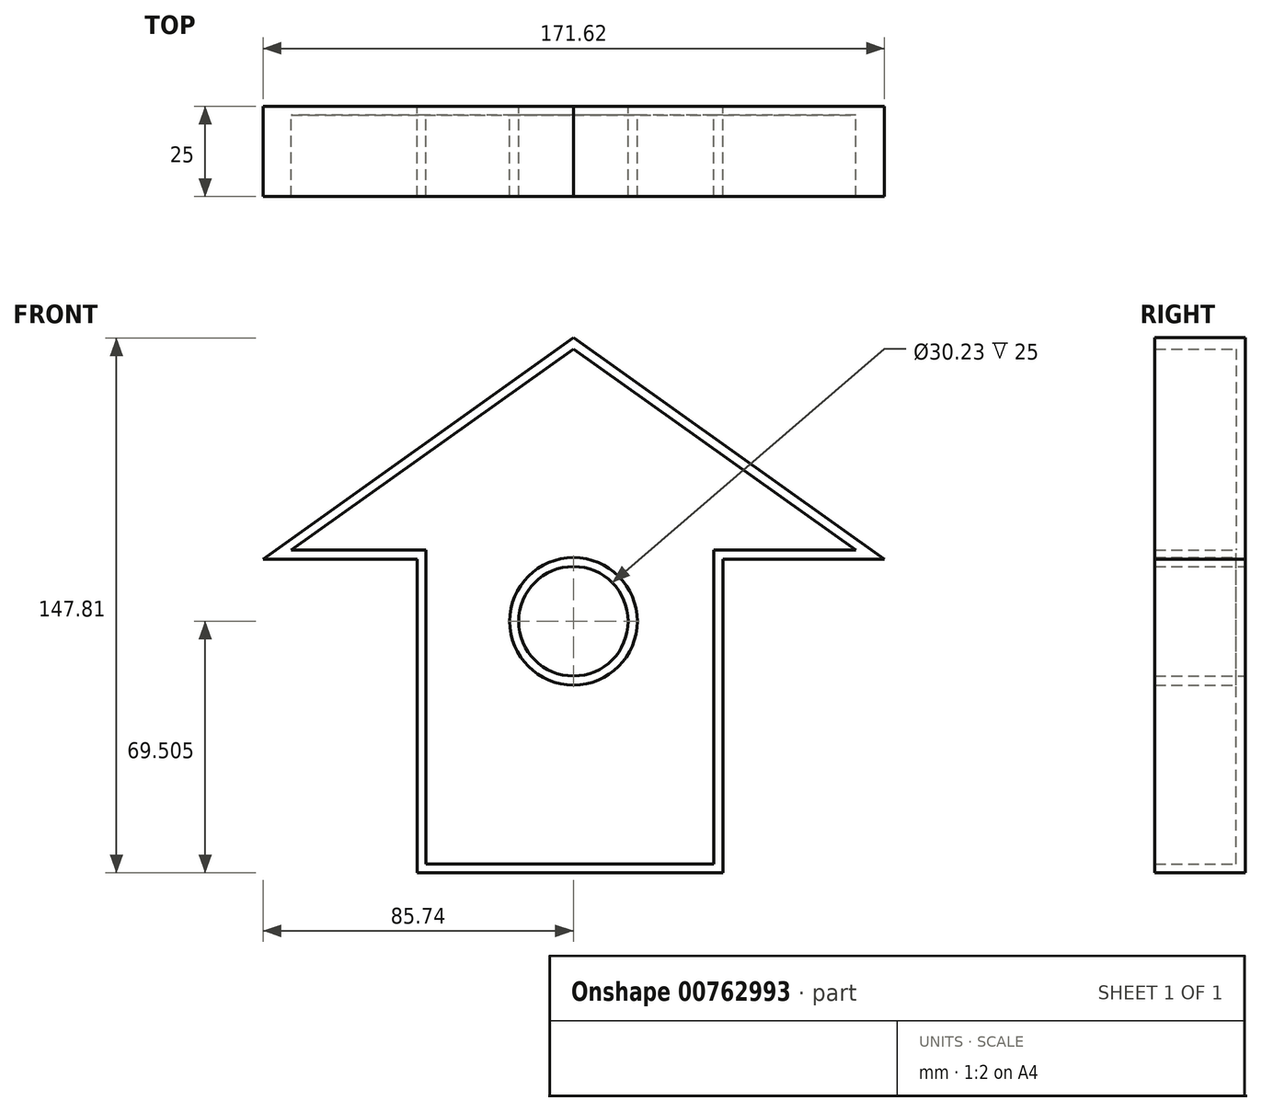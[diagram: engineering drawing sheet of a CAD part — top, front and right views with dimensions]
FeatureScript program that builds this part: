
annotation { "Feature Type Name" : "Feature", "Feature Type Description" : "" }
export const myFeature = defineFeature(function(context is Context, id is Id, definition is map)
    precondition{}
    {
        {
            var Q0;
            Q0=qCreatedBy(makeId("Front.planeOp"),FACE);
            var sketch = newSketch(context, id + "F0", { "sketchPlane" : qUnion([Q0])});
            skLineSegment(sketch, "E0.bottom", {"start": v(41.26, -44.06) * mm, "end": v(-43.22, -44.06) * mm});
            skLineSegment(sketch, "E0.top", {"start": v(41.26, 42.66) * mm, "end": v(-43.22, 42.66) * mm});
            skLineSegment(sketch, "E0.left", {"start": v(41.26, -44.06) * mm, "end": v(41.26, 42.66) * mm});
            skLineSegment(sketch, "E0.right", {"start": v(-43.22, -44.06) * mm, "end": v(-43.22, 42.66) * mm});
            skLineSegment(sketch, "E1", {"start": v(-43.22, 42.66) * mm, "end": v(-85.74, 42.66) * mm});
            skLineSegment(sketch, "E2", {"start": v(-85.74, 42.66) * mm, "end": v(0, 103.75) * mm});
            skLineSegment(sketch, "E3", {"start": v(0, 103.75) * mm, "end": v(85.88, 42.66) * mm});
            skLineSegment(sketch, "E4", {"start": v(85.88, 42.66) * mm, "end": v(41.26, 42.66) * mm});
            skCircle(sketch, "E5", {"center": v(0, 25.44) * mm, "radius": 15.11 * mm});
            skSolve(sketch);
        }
        {
            var Q0;
            Q0 = qSketchRegion(id + "F0", true);
            extrude(context, id + "F1", {"entities" : qUnion([Q0]), "depth" : 25 * mm, "offsetDistance" : 25 * mm});
        }
        {
            var Q0;
            Q0=makeQuery(id+"F1.opExtrude","CAP_FACE",FACE,{"disambiguationData":[OSD([sQuery(id+"F0.wireOp",EDGE,"E0.bottom"),sQuery(id+"F0.wireOp",EDGE,"E0.left"),sQuery(id+"F0.wireOp",EDGE,"E0.right"),sQuery(id+"F0.wireOp",EDGE,"E1"),sQuery(id+"F0.wireOp",EDGE,"E2"),sQuery(id+"F0.wireOp",EDGE,"E3"),sQuery(id+"F0.wireOp",EDGE,"E4"),sQuery(id+"F0.wireOp",EDGE,"E5")])],"isStart":false});
            shell(context, id + "F2", {"entities" : qUnion([Q0]), "thickness" : 2.5 * mm});
        }
    });
